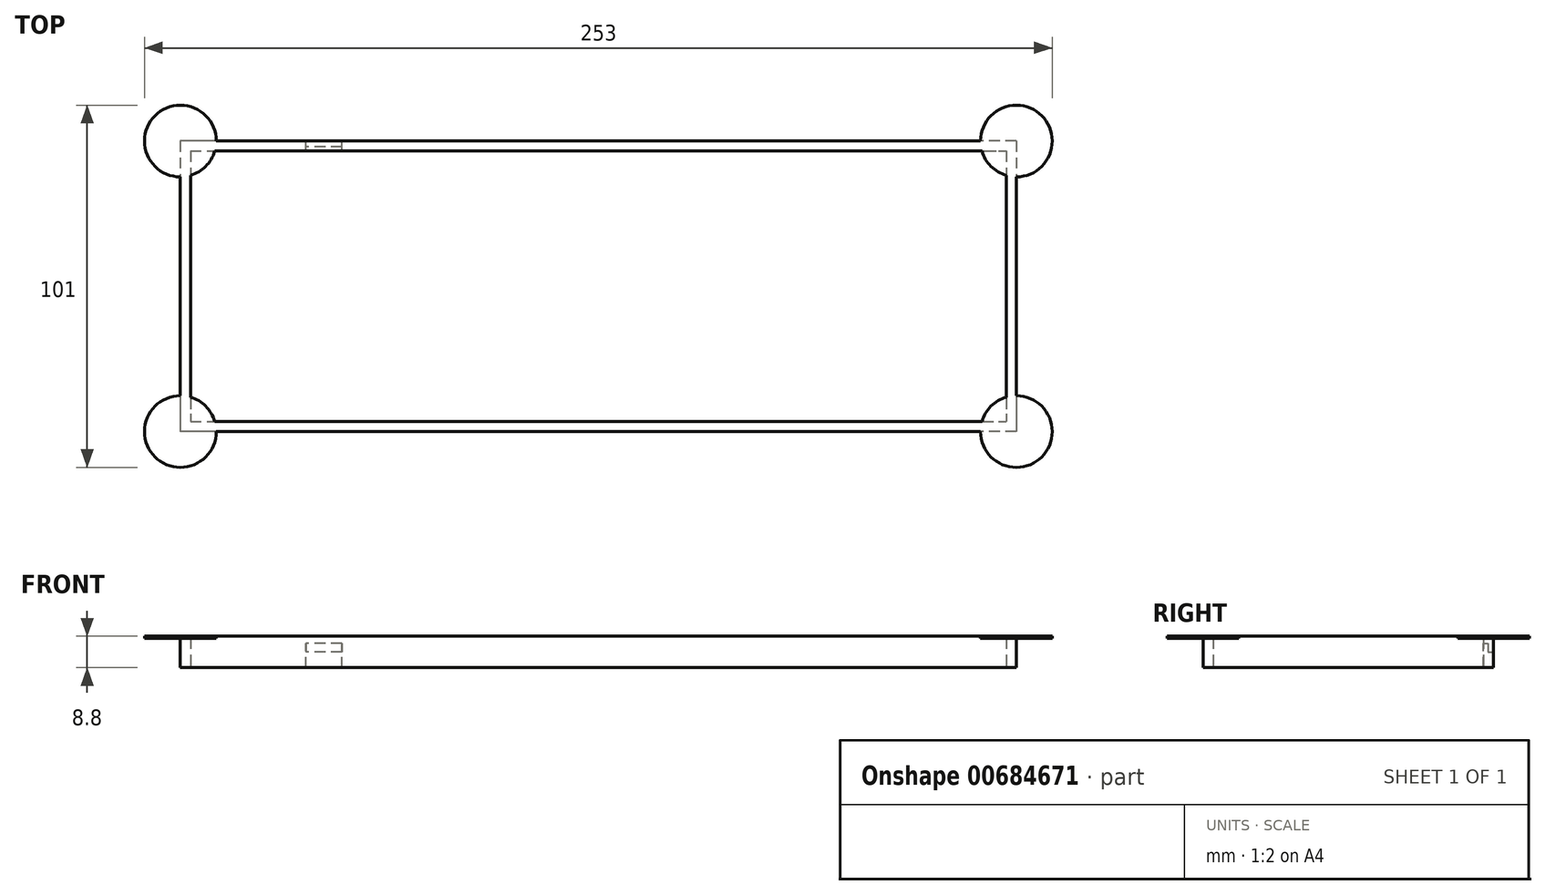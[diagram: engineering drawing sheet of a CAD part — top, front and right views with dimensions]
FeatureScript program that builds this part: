
annotation { "Feature Type Name" : "Feature", "Feature Type Description" : "" }
export const myFeature = defineFeature(function(context is Context, id is Id, definition is map)
    precondition{}
    {
        {
            var Q0;
            Q0=qCreatedBy(makeId("Top.planeOp"),FACE);
            var sketch = newSketch(context, id + "F0", { "sketchPlane" : qUnion([Q0])});
            skLineSegment(sketch, "E0.bottom", {"start": v(116.5, 40.5) * mm, "end": v(-116.5, 40.5) * mm});
            skLineSegment(sketch, "E0.top", {"start": v(116.5, -40.5) * mm, "end": v(-116.5, -40.5) * mm});
            skLineSegment(sketch, "E0.left", {"start": v(116.5, 40.5) * mm, "end": v(116.5, -40.5) * mm});
            skLineSegment(sketch, "E0.right", {"start": v(-116.5, 40.5) * mm, "end": v(-116.5, -40.5) * mm});
            skPoint(sketch, "E0.middle", {"position": v(0, 0) * mm});
            skLineSegment(sketch, "E1.bottom", {"start": v(-113.7, 37.7) * mm, "end": v(113.7, 37.7) * mm});
            skLineSegment(sketch, "E1.top", {"start": v(-113.7, -37.7) * mm, "end": v(113.7, -37.7) * mm});
            skLineSegment(sketch, "E1.left", {"start": v(-113.7, 37.7) * mm, "end": v(-113.7, -37.7) * mm});
            skLineSegment(sketch, "E1.right", {"start": v(113.7, 37.7) * mm, "end": v(113.7, -37.7) * mm});
            skSolve(sketch);
        }
        {
            var Q0;
            Q0=makeQuery(id+"F0.imprint","IMPRINT",FACE,{"disambiguationData":[TD([[makeQuery(id+"F0.imprint","IMPRINT",EDGE,{"derivedFrom":sQuery(id+"F0.wireOp",EDGE,"E0.bottom")}),1.0]])]});
            extrude(context, id + "F1", {"entities" : qUnion([Q0]), "depth" : 8.8 * mm, "offsetDistance" : 25 * mm});
        }
        {
            var Q0;
            Q0=makeQuery(id+"F1.opExtrude","SWEPT_FACE",FACE,{"disambiguationData":[OSD([sQuery(id+"F0.wireOp",EDGE,"E0.bottom")])]});
            var sketch = newSketch(context, id + "F2", { "sketchPlane" : qUnion([Q0])});
            skLineSegment(sketch, "E2.bottom", {"start": v(71.5, 0) * mm, "end": v(81.5, 0) * mm});
            skLineSegment(sketch, "E2.top", {"start": v(71.5, 4.4) * mm, "end": v(81.5, 4.4) * mm});
            skLineSegment(sketch, "E2.left", {"start": v(71.5, 0) * mm, "end": v(71.5, 4.4) * mm});
            skLineSegment(sketch, "E2.right", {"start": v(81.5, 0) * mm, "end": v(81.5, 4.4) * mm});
            skPoint(sketch, "E2.middle", {"position": v(76.5, 2.2) * mm});
            skSolve(sketch);
        }
        {
            var Q0;
            Q0=makeQuery(id+"F2.imprint","IMPRINT",FACE,{"disambiguationData":[TD([[makeQuery(id+"F2.imprint","IMPRINT",EDGE,{"derivedFrom":sQuery(id+"F2.wireOp",EDGE,"E2.bottom")}),1.0]])]});
            extrude(context, id + "F3", {"entities" : qUnion([Q0]), "operationType" : NewBodyOperationType.REMOVE, "oppositeDirection" : true, "depth" : 25 * mm, "offsetDistance" : 25 * mm});
        }
        {
            var Q0;
            Q0=makeQuery(id+"F3.boolean.opBoolean","COPY",FACE,{"derivedFrom":makeQuery(id+"F3.opExtrude","SWEPT_FACE",FACE,{"disambiguationData":[OSD([sQuery(id+"F2.wireOp",EDGE,"E2.top")])]})});
            var sketch = newSketch(context, id + "F4", { "sketchPlane" : qUnion([Q0])});
            skLineSegment(sketch, "E3.bottom", {"start": v(-71.5, -37.7) * mm, "end": v(-81.5, -37.7) * mm});
            skLineSegment(sketch, "E3.top", {"start": v(-71.5, -38.9) * mm, "end": v(-81.5, -38.9) * mm});
            skLineSegment(sketch, "E3.left", {"start": v(-71.5, -37.7) * mm, "end": v(-71.5, -38.9) * mm});
            skLineSegment(sketch, "E3.right", {"start": v(-81.5, -37.7) * mm, "end": v(-81.5, -38.9) * mm});
            skSolve(sketch);
        }
        {
            var Q0;
            Q0=makeQuery(id+"F4.imprint","IMPRINT",FACE,{"disambiguationData":[TD([[makeQuery(id+"F4.imprint","IMPRINT",EDGE,{"derivedFrom":sQuery(id+"F4.wireOp",EDGE,"E3.bottom")}),1.0]])]});
            extrude(context, id + "F5", {"entities" : qUnion([Q0]), "operationType" : NewBodyOperationType.REMOVE, "oppositeDirection" : true, "depth" : 2.4 * mm, "offsetDistance" : 25 * mm});
        }
        {
            var Q0;
            Q0=makeQuery(id+"F1.opExtrude","CAP_FACE",FACE,{"disambiguationData":[OSD([sQuery(id+"F0.wireOp",EDGE,"E0.bottom"),sQuery(id+"F0.wireOp",EDGE,"E0.top"),sQuery(id+"F0.wireOp",EDGE,"E0.left"),sQuery(id+"F0.wireOp",EDGE,"E0.right"),sQuery(id+"F0.wireOp",EDGE,"E1.bottom"),sQuery(id+"F0.wireOp",EDGE,"E1.top"),sQuery(id+"F0.wireOp",EDGE,"E1.left"),sQuery(id+"F0.wireOp",EDGE,"E1.right")])],"isStart":false});
            var sketch = newSketch(context, id + "F6", { "sketchPlane" : qUnion([Q0])});
            skCircle(sketch, "E4", {"center": v(-116.5, 40.5) * mm, "radius": 10 * mm});
            skCircle(sketch, "E5", {"center": v(-116.5, -40.5) * mm, "radius": 10 * mm});
            skCircle(sketch, "E6", {"center": v(116.5, -40.5) * mm, "radius": 10 * mm});
            skCircle(sketch, "E7", {"center": v(116.5, 40.5) * mm, "radius": 10 * mm});
            skSolve(sketch);
        }
        {
            var Q0;
            Q0 = qSketchRegion(id + "F6", true);
            extrude(context, id + "F7", {"entities" : qUnion([Q0]), "operationType" : NewBodyOperationType.ADD, "oppositeDirection" : true, "depth" : .6 * mm, "offsetDistance" : 25 * mm});
        }
    });
